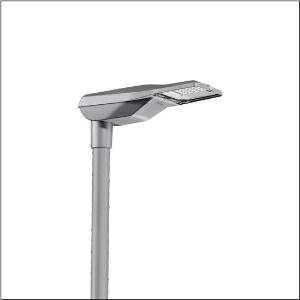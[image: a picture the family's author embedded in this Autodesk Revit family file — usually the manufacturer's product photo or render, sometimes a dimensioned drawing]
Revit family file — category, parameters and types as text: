
# Revit family: streetlight_sl_21_iq_micro___st0_8a_5xe1c31d08cb_88cc
name_source: partatom
category: Lighting Fixtures
units: mm (PartAtom-declared; Revit-internal decimal feet)

## family parameters
Cut with Voids When Loaded = No
Host = Face
Light Source = No
Part Type = Normal
Room Calculation Point = No
Round Connector Dimension = Use Diameter
Shared = No

## types (1)
- --- (1 x LED, 2870 lm, 19.4 W, 3000K)
    Apparent Load = 19 VA
    CIE Flux Codes = 38 75 97 100 100
    Color Rendering = 70
    Color Temperature = 3000K
    Default Elevation = 1800 mm
    Description = Streetlight SL 21 iQ micro, mast luminaire, primary light control with lens, of PMMA, primary optical cover: cover, of toughened safety glass, transparent, light distribution: ST0.8a, light emission: direct distribution, primary light characteristic: asymmetric, installation type: post-top, side-entry, LED, High Power LED, rated luminous flux: 2.870lm, luminous efficacy: 148lm/W, light colour: 730, colour temperature: 3000K, control: Auto-Match, Temp-Guard, Lumen-Switch, Night-Set, Smart-Wire, Light-Fading, Desk-Remote (wireless, voltage-free reading and setting of iQ features in the workshop via application-optimized NFC function/RFID function), optimised constant luminous flux control (CLO 2.0), presetting dimming linear, mains connection: 220..240V, AC, 50/60Hz, start of lifetime: 19W, end of service life: 20W, reduction: 10W, luminaire housing, of diecast aluminium, powder-coated, Siteco® metallic grey (DB 702S), corrosivity category C5 mid according to DIN EN ISO 12944, please order mast flange separately, inclination adjustable: 0°, 5°, 10°, 15°, sealing non-destructively replaceable, multi-level sealing system, length: 528mm, width: 235mm, height: 110mm, mast flange for spigot size: 42mm (side-entry): 5XC10008XM4, 60/48mm (side-entry/post-top): 5XC10108XM2, 76/60mm (side-entry/post-top): 5XC10108XM1, protection rating (complete): IP66, insulation class (complete): insulation class II (safety insulation), certification: CE, ENEC, ENEC+, VDE, impact resistance: IK09, permissible operating ambient temperature for outdoor applications: -40..+50°C, standard-compliant lighting for roads and squares, packaging unit: 1 piece

Light Distribution: ST0.8a
    Height = 110 mm
    Lamp = 1 x LED
    Lamp Light Flux = 2870 lm
    Lamp Power = 19.4 W
    Lamp count = 1
    Length = 528 mm
    Luminous efficacy = 148 lm/W
    Manufacturer = Siteco
    ModVariant = No
    Model = 5XE1C31D08CB
    Number of Poles = 1
    OnlyDefault = Yes
    Power Factor = 1
    Product Name = Streetlight SL 21 iQ micro | ST0.8a
    Product group = mast luminaire | pylon top
    ProductGroupID = 6100
    Protection Class = Protection class II
    Protection Degree = IP 66
    RLX_Detail_Level = 1
    RLX_Emergency_Light_Flux = 0 lm
    RLX_Emergency_Type = 0
    RLX_Emergency_Type_DB = No
    RlxData = <blob elided: 98865 chars, md5=2d12d68a>
    Socket = socket
    Standby Power = 0 W
    System Light Flux = 2870 lm
    System Power = 19 W
    Type Comments = factory setting: luminous flux: 100 % | dim-lin: 254 | 387 mA
    Type Image = l_1006881.jpg
    URL = http://relux.com
    VarID = @adj_069789
    Voltage = 0 V
    Weight = 0.00 kg
    Width = 235 mm

## geometry (parser evidence)
native form markers: Blend x4, Sweep x12
no freeform markers — native parametric forms only
